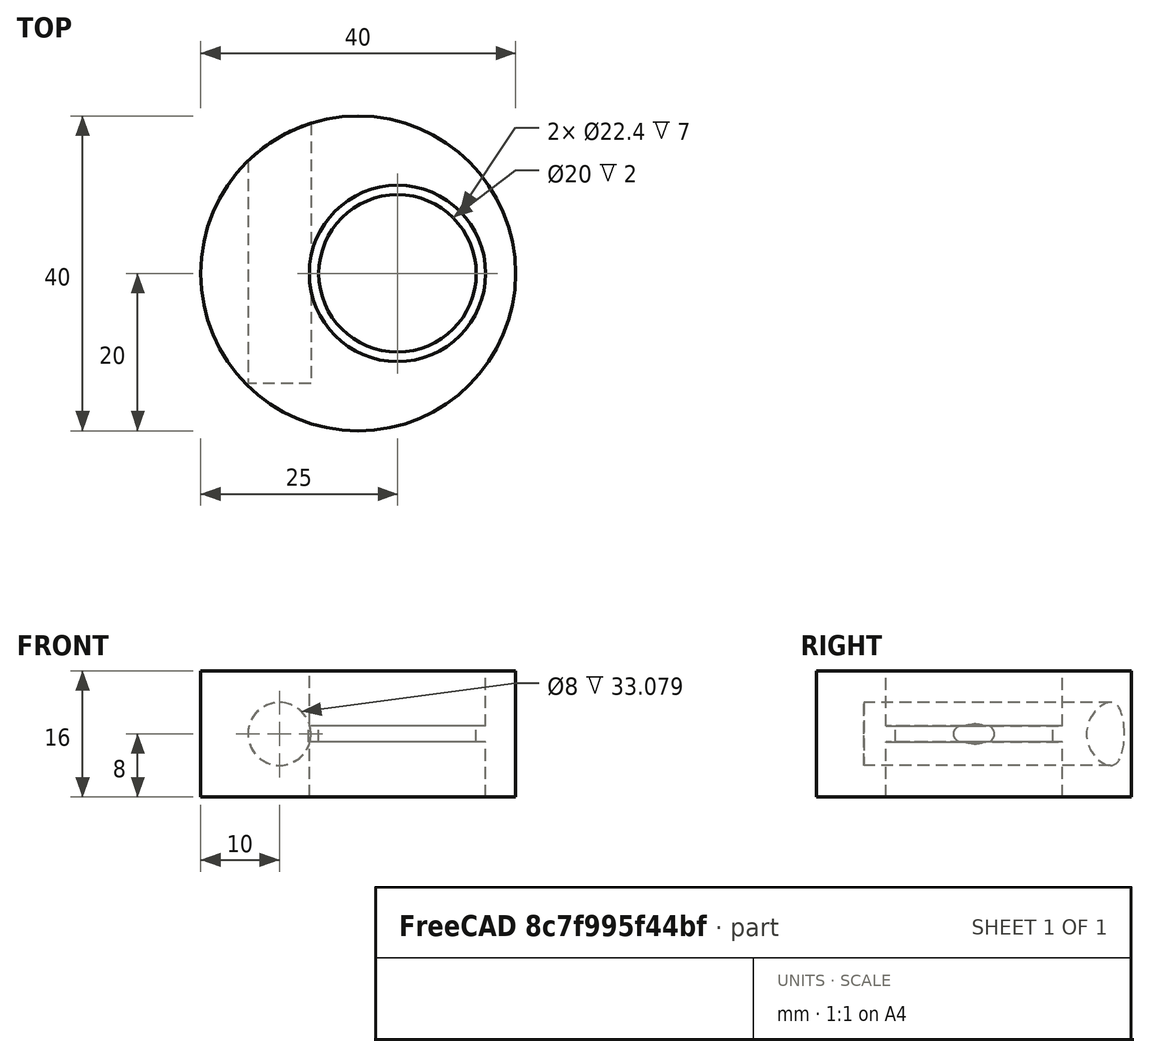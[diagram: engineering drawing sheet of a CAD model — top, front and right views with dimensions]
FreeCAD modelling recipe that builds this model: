
FCSTD DOCUMENT  (FreeCAD 0.15R4671 (Git))
Label: caster-eccentric-3
License: All rights reserved
LicenseURL: http://en.wikipedia.org/wiki/All_rights_reserved
objects: Part::Cylinder×5, Part::Cut×3, Part::MultiFuse×1
note: 9 computed .brp shape members not serialized (recipe doc carries the construction recipe); baked Part::Feature solids carry a one-line shape summary decoded from their .brp

FEATURE [Part::Cylinder] Cylinder
  Angle = 360
  Height = 16
  Radius = 20
FEATURE [Part::Cylinder] Cylinder001
  Angle = 360
  Height = 16
  Placement = pos=(5,0,0) rot=(0,0,1;0rad)
  Radius = 11.2
FEATURE [Part::Cylinder] Cylinder002
  Angle = 360
  Height = 40
  Placement = pos=(-10,26,8) rot=(1,0,0;1.5708rad)
  Radius = 4
FEATURE [Part::Cut] Cut
  Base = -> Cylinder
  Tool = -> Cylinder001
FEATURE [Part::Cut] Cut001
  Base = -> Cut
  Tool = -> Cylinder002
FEATURE [Part::Cylinder] Cylinder003
  Angle = 360
  Height = 2
  Placement = pos=(5,0,7) rot=(0,0,1;0rad)
  Radius = 11.3
FEATURE [Part::MultiFuse] Fusion
  Shapes = -> [Cut001,Cylinder003]
FEATURE [Part::Cylinder] Cylinder004
  Angle = 360
  Height = 10
  Placement = pos=(5,0,0) rot=(0,0,1;0rad)
  Radius = 10
FEATURE [Part::Cut] Cut002
  Base = -> Fusion
  Tool = -> Cylinder004
